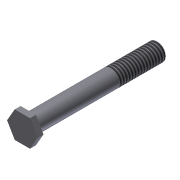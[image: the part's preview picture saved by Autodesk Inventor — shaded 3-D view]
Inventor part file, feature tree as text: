
AUTODESK INVENTOR PART (.ipt)
format: ipt  version: 2013 (Build 170138000, 138)  size: 92,672 bytes
history: native  units: in
note: dims shown in document units (in); Inventor stores cm internally (conversion verified against a paired STEP export)
features: extrude x2, sketch x2, thread x1, chamfer x1
ambient origin geometry x8: Origin, YZ Plane, XZ Plane, XY Plane, X Axis, Y Axis, Z Axis, Center Point
bodies: Solid1 (feature_tree)
feature tree (6):
  extrude  "Extrusion1"  Depth=2.75in TaperAngle=0.0deg
  extrude  "Extrusion2"  Depth=0.125in TaperAngle=0.0deg
  thread  "Thread1"  [1 undecoded]
  chamfer  "Chamfer1"  Distance=0.02in Angle=45.0deg
  sketch  "Sketch1"  dims[d0=0.375in d1=2.75in d2=0.0in]
  sketch  "Sketch2"  dims[d3=0.5625in d4=0.125in d5=0.0in d6=1.0in d7=0.0in d8=0.02in d9=0.125in d10=45.0deg]
note: 1 required parameter value undecoded (feature->parameter linkage not recoverable at this tier; creation-order binding heuristic only, values carry confidence <= 0.55)
